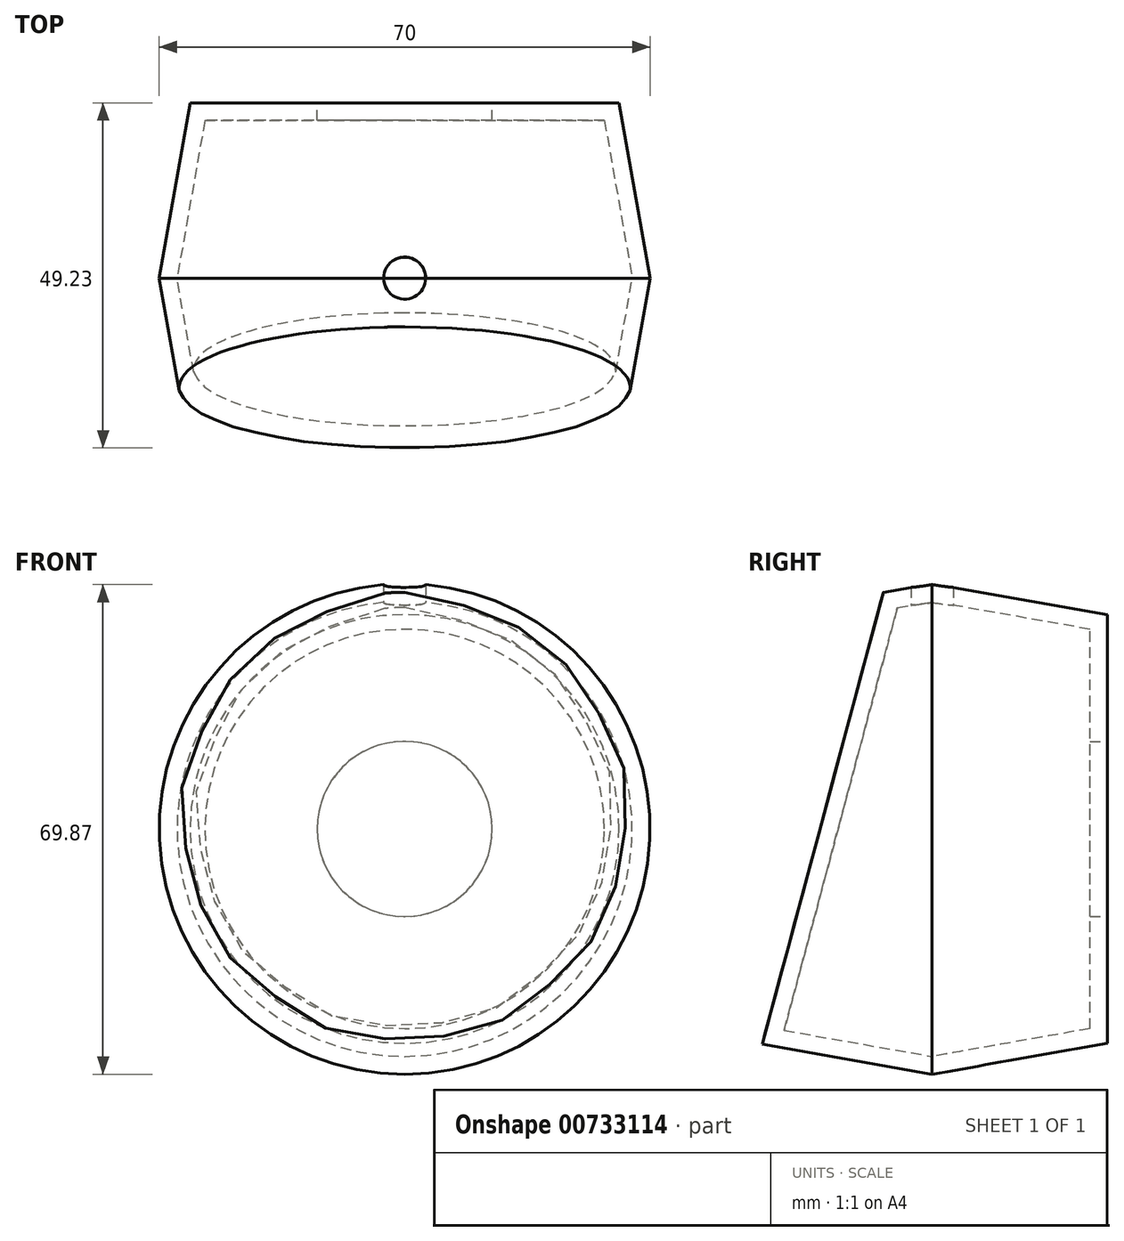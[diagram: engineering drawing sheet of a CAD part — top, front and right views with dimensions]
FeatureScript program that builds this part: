
annotation { "Feature Type Name" : "Feature", "Feature Type Description" : "" }
export const myFeature = defineFeature(function(context is Context, id is Id, definition is map)
    precondition{}
    {
        {
            var Q0;
            Q0=qCreatedBy(makeId("Front.planeOp"),FACE);
            var sketch = newSketch(context, id + "F0", { "sketchPlane" : qUnion([Q0])});
            skCircle(sketch, "E0", {"center": v(0, 0) * mm, "radius": 35 * mm});
            skSolve(sketch);
        }
        {
            var Q0;
            Q0=makeQuery(id+"F0.imprint","IMPRINT",FACE,{"disambiguationData":[TD([[makeQuery(id+"F0.imprint","IMPRINT",EDGE,{"derivedFrom":sQuery(id+"F0.wireOp",EDGE,"E0")}),1.0]])]});
            var Q1;
            Q1=sQuery(id+"F0.wireOp",EDGE,"E0");
            extrude(context, id + "F1", {"entities" : qUnion([Q0]), "surfaceEntities" : qUnion([Q1]), "endBound" : BoundingType.SYMMETRIC, "depth" : 50 * mm, "offsetDistance" : 25 * mm, "hasDraft" : true, "draftAngle" : 10 * degree, "draftPullDirection" : true});
        }
        {
            var Q0;
            Q0=qCreatedBy(makeId("Right.planeOp"),FACE);
            var sketch = newSketch(context, id + "F2", { "sketchPlane" : qUnion([Q0])});
            skLineSegment(sketch, "E1", {"start": v(-5.75, 38.26) * mm, "end": v(-29.22, -49.32) * mm});
            skLineSegment(sketch, "E2", {"start": v(-5.75, 38.26) * mm, "end": v(-37.5, 38.26) * mm});
            skLineSegment(sketch, "E3", {"start": v(-37.5, 38.26) * mm, "end": v(-37.5, -49.69) * mm});
            skLineSegment(sketch, "E4", {"start": v(-29.22, -49.32) * mm, "end": v(-37.5, -49.69) * mm});
            skLineSegment(sketch, "E5", {"start": v(-99.85, 0) * mm, "end": v(0, 0) * mm, "construction": true});
            skSolve(sketch);
        }
        {
            var Q0;
            Q0=makeQuery(id+"F2.imprint","IMPRINT",FACE,{"disambiguationData":[TD([[makeQuery(id+"F2.imprint","IMPRINT",EDGE,{"derivedFrom":sQuery(id+"F2.wireOp",EDGE,"E1")}),-1.0]])]});
            extrude(context, id + "F3", {"entities" : qUnion([Q0]), "operationType" : NewBodyOperationType.REMOVE, "endBound" : BoundingType.SYMMETRIC, "oppositeDirection" : true, "depth" : 80 * mm, "offsetDistance" : 25 * mm});
        }
        {
            var Q0;
            Q0=makeQuery(id+"F1.opExtrude","CAP_FACE",FACE,{"disambiguationData":[OSD([sQuery(id+"F0.wireOp",EDGE,"E0")])],"isStart":true});
            var Q1;
            Q1=makeQuery(id+"F1.*.split.splitOp","SPLIT",FACE,{"derivedFrom":makeQuery(id+"F1.opExtrude","SWEPT_FACE",FACE,{"disambiguationData":[OSD([sQuery(id+"F0.wireOp",EDGE,"E0")])]}),"isFromBackBody":true});
            var Q2;
            Q2=makeQuery(id+"F1.*.split.splitOp","SPLIT",FACE,{"derivedFrom":makeQuery(id+"F1.opExtrude","SWEPT_FACE",FACE,{"disambiguationData":[OSD([sQuery(id+"F0.wireOp",EDGE,"E0")])]})});
            var Q3;
            Q3=makeQuery(id+"F3.boolean.opBoolean","COPY",FACE,{"derivedFrom":makeQuery(id+"F3.opExtrude","SWEPT_FACE",FACE,{"disambiguationData":[OSD([sQuery(id+"F2.wireOp",EDGE,"E1")])]})});
            var Q4;
            Q4=makeQuery(id+"F1.*.split.splitOp","SPLIT",BODY,{"derivedFrom":makeQuery(id+"F1.opExtrude","SWEPT_BODY",BODY,{"disambiguationData":[OSD([sQuery(id+"F0.wireOp",EDGE,"E0")])]})});
            shell(context, id + "F4", {"isHollow" : true, "entities" : qUnion([Q0, Q1, Q2, Q3]), "parts" : qUnion([Q4]), "thickness" : 2.5 * mm});
        }
        {
            var Q0;
            Q0=qCreatedBy(makeId("Top.planeOp"),FACE);
            var sketch = newSketch(context, id + "F5", { "sketchPlane" : qUnion([Q0])});
            skPoint(sketch, "E6", {"position": v(0, 0) * mm});
            skSolve(sketch);
        }
        {
            var Q0;
            Q0=sQuery(id+"F5.wireOp",VERTEX,"E6");
            var Q1;
            Q1=makeQuery(id+"F1.*.split.splitOp","SPLIT",BODY,{"derivedFrom":makeQuery(id+"F1.opExtrude","SWEPT_BODY",BODY,{"disambiguationData":[OSD([sQuery(id+"F0.wireOp",EDGE,"E0")])]})});
            hole(context, id + "F6", {"style" : HoleStyle.SIMPLE, "endStyle" : HoleEndStyle.THROUGH, "oppositeDirection" : true, "holeDiameter" : 6 * mm, "majorDiameter" : 5 * mm, "isTappedThrough" : true, "tappedDepth" : 12 * mm, "tapClearance" : 3, "locations" : qUnion([Q0]), "scope" : qUnion([Q1])});
        }
        {
            var Q0;
            Q0=makeQuery(id+"F1.opExtrude","CAP_FACE",FACE,{"disambiguationData":[OSD([sQuery(id+"F0.wireOp",EDGE,"E0")])],"isStart":true});
            var sketch = newSketch(context, id + "F7", { "sketchPlane" : qUnion([Q0])});
            skCircle(sketch, "E7", {"center": v(0, 0) * mm, "radius": 12.5 * mm});
            skSolve(sketch);
        }
        {
            var Q0;
            Q0=makeQuery(id+"F7.imprint","IMPRINT",FACE,{"disambiguationData":[TD([[makeQuery(id+"F7.imprint","IMPRINT",EDGE,{"derivedFrom":sQuery(id+"F7.wireOp",EDGE,"E7")}),1.0]])]});
            extrude(context, id + "F8", {"entities" : qUnion([Q0]), "operationType" : NewBodyOperationType.REMOVE, "endBound" : BoundingType.UP_TO_NEXT, "oppositeDirection" : true, "depth" : 25 * mm, "offsetDistance" : 25 * mm});
        }
    });
